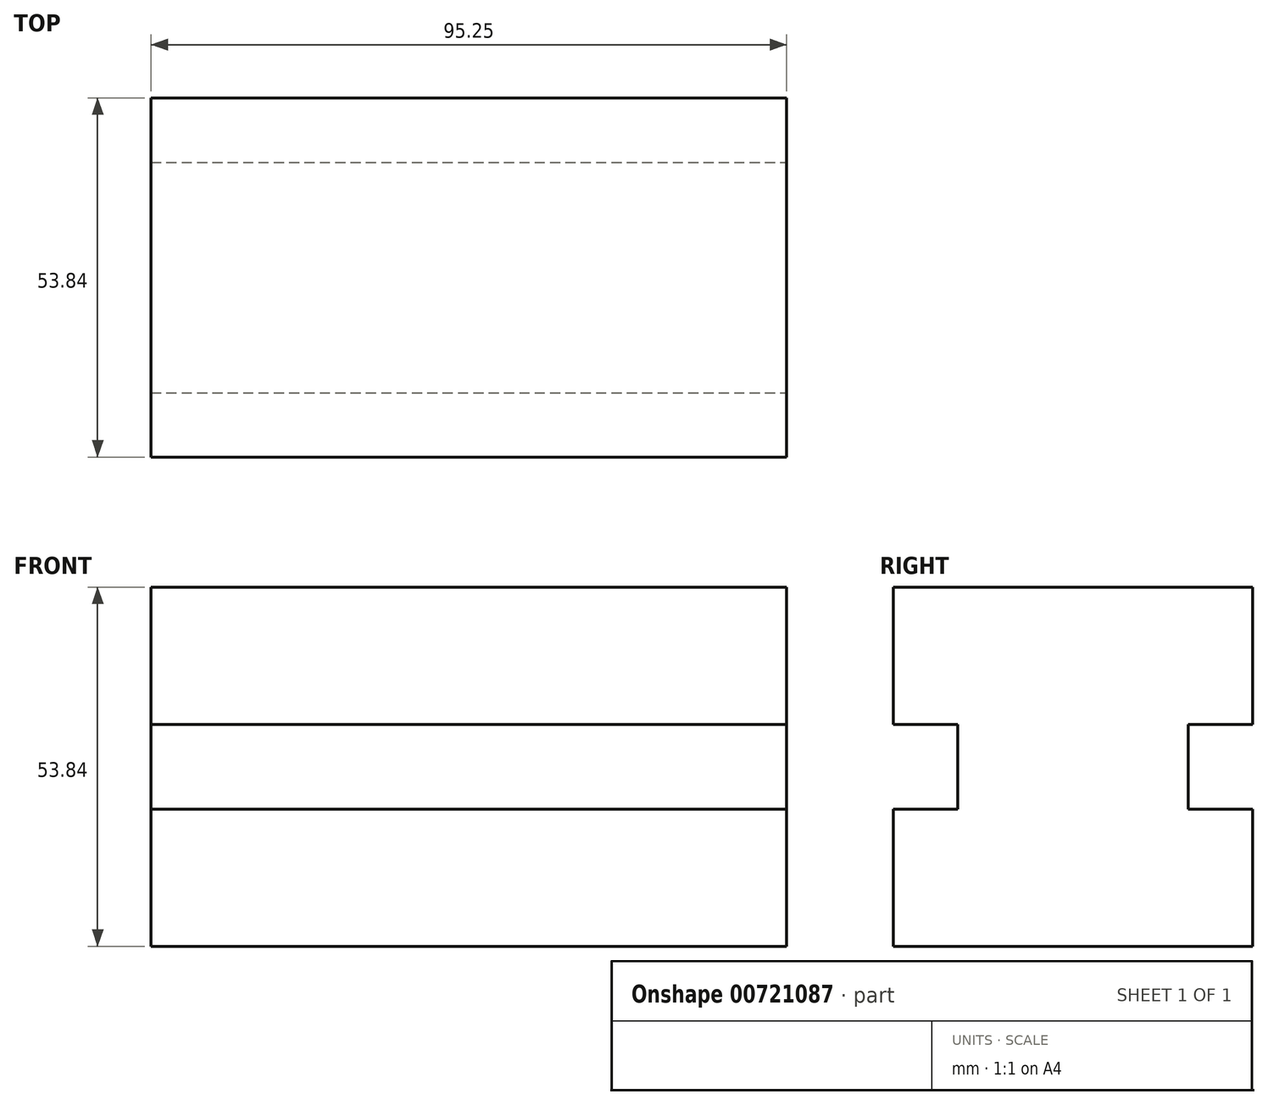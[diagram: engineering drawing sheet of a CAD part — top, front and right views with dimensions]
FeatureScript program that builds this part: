
annotation { "Feature Type Name" : "Feature", "Feature Type Description" : "" }
export const myFeature = defineFeature(function(context is Context, id is Id, definition is map)
    precondition{}
    {
        {
            var Q0;
            Q0=qCreatedBy(makeId("Right.planeOp"),FACE);
            var sketch = newSketch(context, id + "F0", { "sketchPlane" : qUnion([Q0])});
            skLineSegment(sketch, "E0.bottom", {"start": v(-26.92, 26.92) * mm, "end": v(26.92, 26.92) * mm});
            skLineSegment(sketch, "E0.top", {"start": v(-26.92, -26.92) * mm, "end": v(26.92, -26.92) * mm});
            skLineSegment(sketch, "E0.left", {"start": v(-26.92, 26.92) * mm, "end": v(-26.92, 6.35) * mm});
            skLineSegment(sketch, "E0.right", {"start": v(26.92, 26.92) * mm, "end": v(26.92, 6.35) * mm});
            skPoint(sketch, "E0.middle", {"position": v(0, 0) * mm});
            skLineSegment(sketch, "E1.bottom", {"start": v(-26.92, 6.35) * mm, "end": v(-17.27, 6.35) * mm});
            skLineSegment(sketch, "E1.top", {"start": v(-26.92, -6.35) * mm, "end": v(-17.27, -6.35) * mm});
            skLineSegment(sketch, "E1.right", {"start": v(-17.27, 6.35) * mm, "end": v(-17.27, -6.35) * mm});
            skLineSegment(sketch, "E2", {"start": v(0, 33.6) * mm, "end": v(0, -50.36) * mm, "construction": true});
            skLineSegment(sketch, "E3.MirrorCS", {"start": v(26.92, 6.35) * mm, "end": v(17.27, 6.35) * mm});
            skLineSegment(sketch, "E4.MirrorCS", {"start": v(17.27, 6.35) * mm, "end": v(17.27, -6.35) * mm});
            skLineSegment(sketch, "E5.MirrorCS", {"start": v(26.92, -6.35) * mm, "end": v(17.27, -6.35) * mm});
            skLineSegment(sketch, "E6.trimOffspring", {"start": v(-26.92, -6.35) * mm, "end": v(-26.92, -26.92) * mm});
            skLineSegment(sketch, "E7.trimOffspring", {"start": v(26.92, -6.35) * mm, "end": v(26.92, -26.92) * mm});
            skSolve(sketch);
        }
        {
            var Q0;
            Q0=makeQuery(id+"F0.imprint","IMPRINT",FACE,{"disambiguationData":[TD([[makeQuery(id+"F0.imprint","IMPRINT",EDGE,{"derivedFrom":sQuery(id+"F0.wireOp",EDGE,"E0.bottom")}),-1.0]])]});
            extrude(context, id + "F1", {"entities" : qUnion([Q0]), "oppositeDirection" : true, "depth" : 95.25 * mm, "offsetDistance" : 25.4 * mm});
        }
    });
